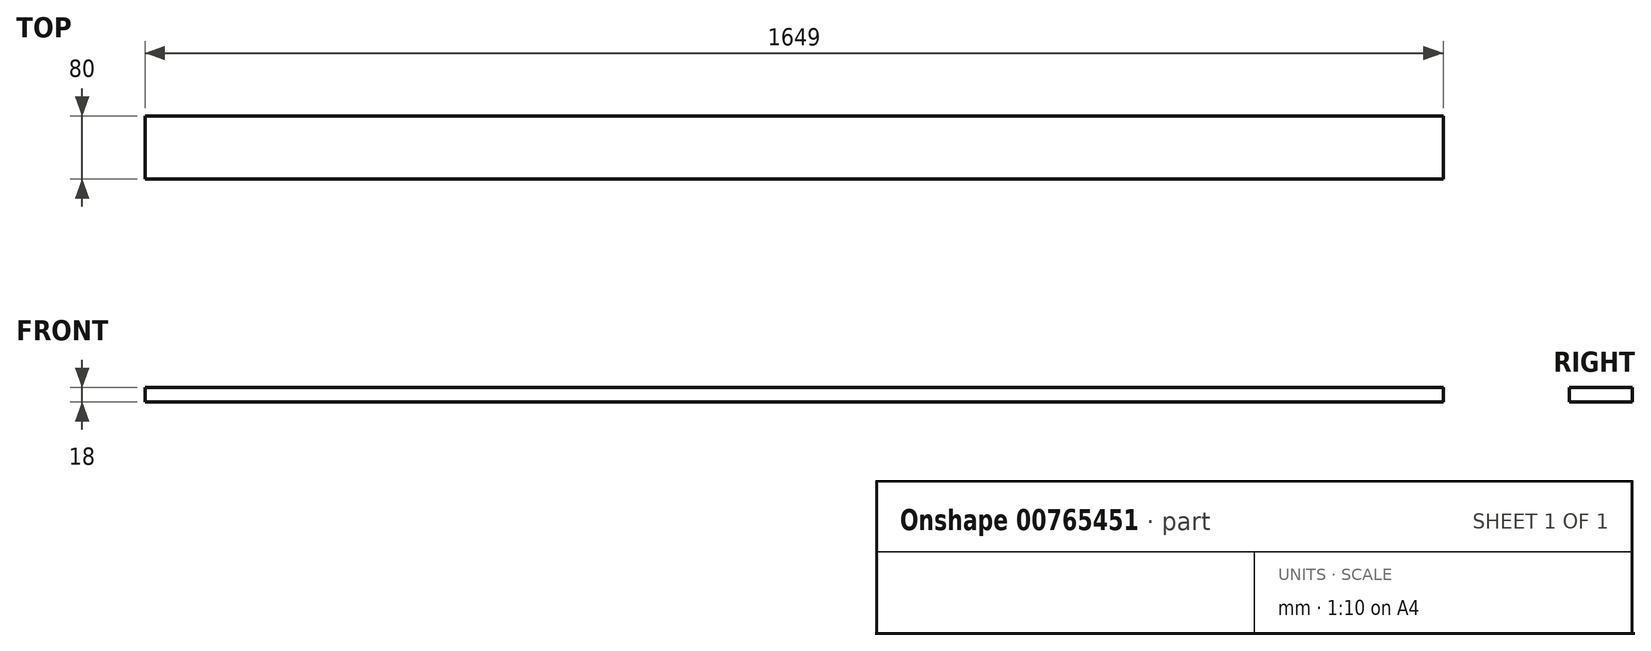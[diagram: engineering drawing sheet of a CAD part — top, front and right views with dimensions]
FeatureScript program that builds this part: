
annotation { "Feature Type Name" : "Feature", "Feature Type Description" : "" }
export const myFeature = defineFeature(function(context is Context, id is Id, definition is map)
    precondition{}
    {
        {
            var Q0;
            Q0=qCreatedBy(makeId("Top.planeOp"),FACE);
            var sketch = newSketch(context, id + "F0", { "sketchPlane" : qUnion([Q0])});
            skLineSegment(sketch, "E0.bottom", {"start": v(-824.5, -40) * mm, "end": v(824.5, -40) * mm});
            skLineSegment(sketch, "E0.top", {"start": v(-824.5, 40) * mm, "end": v(824.5, 40) * mm});
            skLineSegment(sketch, "E0.left", {"start": v(-824.5, -40) * mm, "end": v(-824.5, 40) * mm});
            skLineSegment(sketch, "E0.right", {"start": v(824.5, -40) * mm, "end": v(824.5, 40) * mm});
            skPoint(sketch, "E0.middle", {"position": v(0, 0) * mm});
            skSolve(sketch);
        }
        {
            var Q0;
            Q0 = qSketchRegion(id + "F0", true);
            extrude(context, id + "F1", {"entities" : qUnion([Q0]), "depth" : 18 * mm, "offsetDistance" : 25 * mm});
        }
    });
